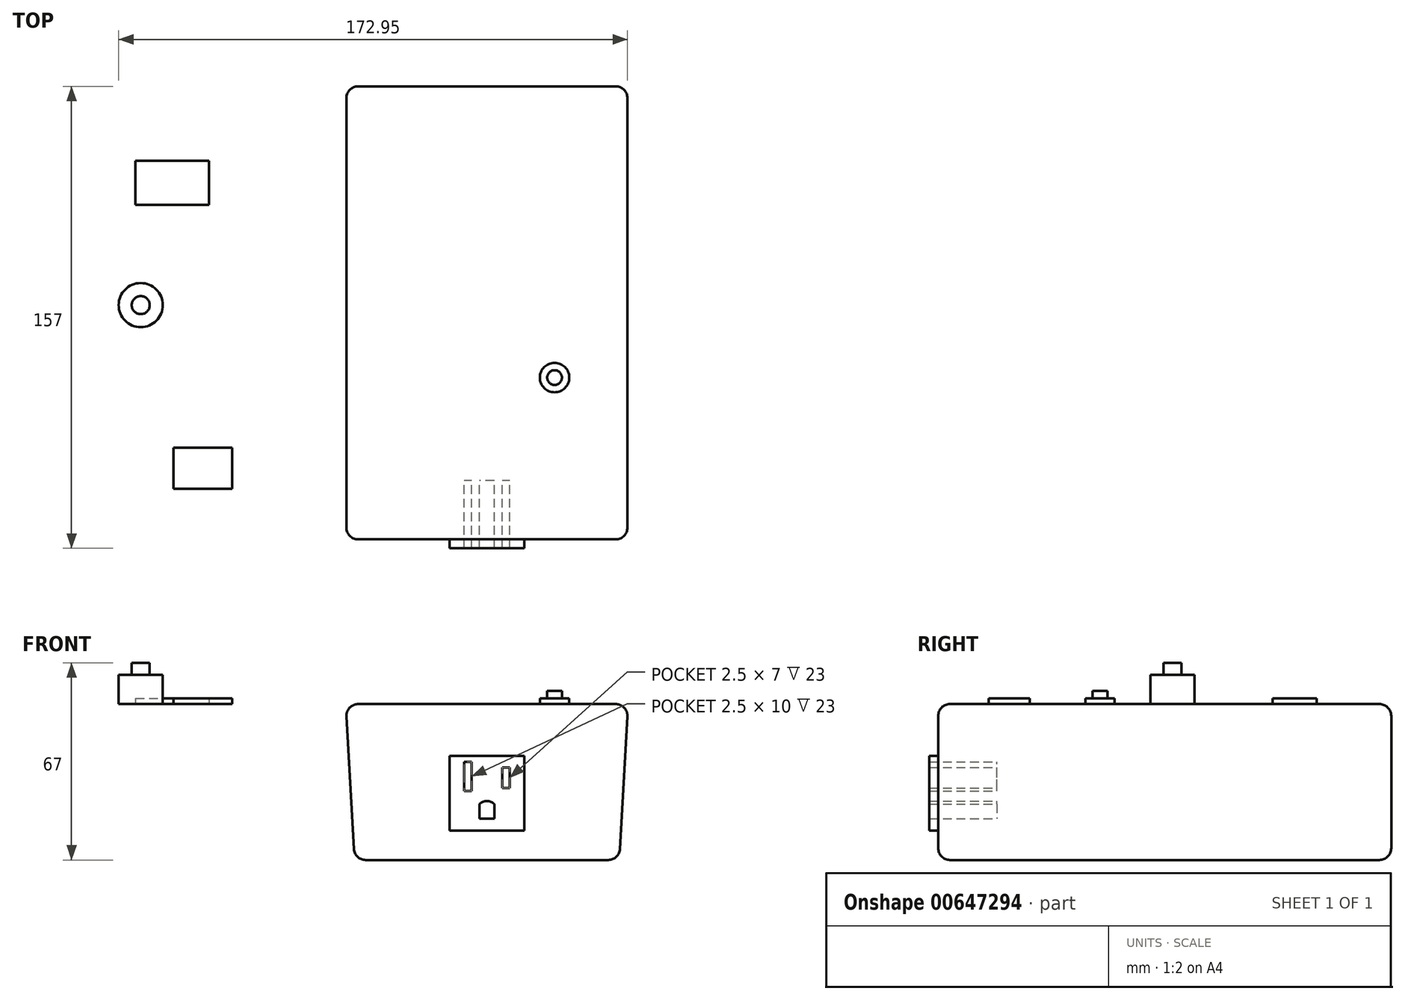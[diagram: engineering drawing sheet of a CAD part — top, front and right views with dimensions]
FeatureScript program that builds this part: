
annotation { "Feature Type Name" : "Feature", "Feature Type Description" : "" }
export const myFeature = defineFeature(function(context is Context, id is Id, definition is map)
    precondition{}
    {
        {
            var Q0;
            Q0=qCreatedBy(makeId("Front.planeOp"),FACE);
            var sketch = newSketch(context, id + "F0", { "sketchPlane" : qUnion([Q0])});
            skLineSegment(sketch, "E0", {"start": v(-48, 0) * mm, "end": v(48, 0) * mm});
            skLineSegment(sketch, "E1", {"start": v(-45, -53) * mm, "end": v(45, -53) * mm});
            skLineSegment(sketch, "E2", {"start": v(-48, 0) * mm, "end": v(-45, -53) * mm});
            skLineSegment(sketch, "E3", {"start": v(48, 0) * mm, "end": v(45, -53) * mm});
            skPoint(sketch, "E4", {"position": v(0, 0) * mm});
            skPoint(sketch, "E5", {"position": v(46.5, -26.5) * mm});
            skPoint(sketch, "E6", {"position": v(-46.5, -26.5) * mm});
            skPoint(sketch, "E7", {"position": v(0, -53) * mm});
            skLineSegment(sketch, "E8", {"start": v(0, 0) * mm, "end": v(0, -53) * mm, "construction": true});
            skLineSegment(sketch, "E9", {"start": v(46.5, -26.5) * mm, "end": v(-46.5, -26.5) * mm, "construction": true});
            skSolve(sketch);
        }
        {
            var Q0;
            Q0 = qSketchRegion(id + "F0", true);
            extrude(context, id + "F1", {"entities" : qUnion([Q0]), "depth" : 154 * mm, "offsetDistance" : 25 * mm});
        }
        {
            var Q0;
            Q0=makeQuery(id+"F1.opExtrude","SWEPT_FACE",FACE,{"disambiguationData":[OSD([sQuery(id+"F0.wireOp",EDGE,"E0")])]});
            var sketch = newSketch(context, id + "F2", { "sketchPlane" : qUnion([Q0])});
            skCircle(sketch, "E10", {"center": v(-23, -99) * mm, "radius": 7.5 * mm});
            skCircle(sketch, "E11", {"center": v(-23, -99) * mm, "radius": 3.06 * mm});
            skCircle(sketch, "E12", {"center": v(23, -99) * mm, "radius": 5 * mm});
            skCircle(sketch, "E13", {"center": v(23, -99) * mm, "radius": 2.5 * mm});
            skLineSegment(sketch, "E14.bottom", {"start": v(-10, -120) * mm, "end": v(10, -120) * mm});
            skLineSegment(sketch, "E14.top", {"start": v(-10, -134) * mm, "end": v(10, -134) * mm});
            skLineSegment(sketch, "E14.left", {"start": v(-10, -120) * mm, "end": v(-10, -134) * mm});
            skLineSegment(sketch, "E14.right", {"start": v(10, -120) * mm, "end": v(10, -134) * mm});
            skLineSegment(sketch, "E15", {"start": v(10, -127) * mm, "end": v(48, -127) * mm, "construction": true});
            skLineSegment(sketch, "E16", {"start": v(-10, -127) * mm, "end": v(-48, -127) * mm, "construction": true});
            skLineSegment(sketch, "E17.bottom", {"start": v(-12.5, -35) * mm, "end": v(12.5, -35) * mm});
            skLineSegment(sketch, "E17.top", {"start": v(-12.5, -50) * mm, "end": v(12.5, -50) * mm});
            skLineSegment(sketch, "E17.left", {"start": v(-12.5, -35) * mm, "end": v(-12.5, -50) * mm});
            skLineSegment(sketch, "E17.right", {"start": v(12.5, -35) * mm, "end": v(12.5, -50) * mm});
            skLineSegment(sketch, "E18", {"start": v(12.5, -42.5) * mm, "end": v(48, -42.5) * mm, "construction": true});
            skLineSegment(sketch, "E19", {"start": v(-12.5, -42.5) * mm, "end": v(-48, -42.5) * mm, "construction": true});
            skSolve(sketch);
        }
        {
            var Q0;
            Q0=makeQuery(id+"F2.imprint","IMPRINT",FACE,{"disambiguationData":[TD([[makeQuery(id+"F2.imprint","IMPRINT",EDGE,{"derivedFrom":sQuery(id+"F2.wireOp",EDGE,"E13")}),1.0]])]});
            extrude(context, id + "F3", {"entities" : qUnion([Q0]), "operationType" : NewBodyOperationType.ADD, "depth" : 4.5 * mm, "offsetDistance" : 25 * mm});
        }
        {
            var Q0;
            Q0=makeQuery(id+"F2.imprint","IMPRINT",FACE,{"disambiguationData":[TD([[makeQuery(id+"F2.imprint","IMPRINT",EDGE,{"derivedFrom":sQuery(id+"F2.wireOp",EDGE,"E12")}),1.0]])]});
            extrude(context, id + "F4", {"entities" : qUnion([Q0]), "operationType" : NewBodyOperationType.ADD, "depth" : 2 * mm, "offsetDistance" : 25 * mm});
        }
        {
            var Q0;
            Q0=makeQuery(id+"F2.imprint","IMPRINT",FACE,{"disambiguationData":[TD([[makeQuery(id+"F2.imprint","IMPRINT",EDGE,{"derivedFrom":sQuery(id+"F2.wireOp",EDGE,"E10")}),1.0]])]});
            extrude(context, id + "F5", {"entities" : qUnion([Q0]), "operationType" : NewBodyOperationType.REMOVE, "depth" : 2 * mm, "offsetDistance" : 25 * mm});
        }
        {
            var Q0;
            Q0=makeQuery(id+"F1.opExtrude","SWEPT_EDGE",EDGE,{"disambiguationData":[OSD([sQuery(id+"F0.wireOp",EDGE,"E1"),sQuery(id+"F0.wireOp",EDGE,"E2")])]});
            var Q1;
            Q1=makeQuery(id+"F1.opExtrude","CAP_EDGE",EDGE,{"disambiguationData":[OSD([sQuery(id+"F0.wireOp",EDGE,"E1")])],"isStart":false});
            var Q2;
            Q2=makeQuery(id+"F1.opExtrude","SWEPT_EDGE",EDGE,{"disambiguationData":[OSD([sQuery(id+"F0.wireOp",EDGE,"E1"),sQuery(id+"F0.wireOp",EDGE,"E3")])]});
            var Q3;
            Q3=makeQuery(id+"F1.opExtrude","CAP_EDGE",EDGE,{"disambiguationData":[OSD([sQuery(id+"F0.wireOp",EDGE,"E1")])],"isStart":true});
            fillet(context, id + "F6", {"entities" : qUnion([Q0, Q1, Q2, Q3]), "radius" : 4 * mm, "tangentPropagation" : true, "allowEdgeOverflow" : false});
        }
        {
            var Q0;
            Q0=makeQuery(id+"F1.opExtrude","CAP_EDGE",EDGE,{"disambiguationData":[OSD([sQuery(id+"F0.wireOp",EDGE,"E0")])],"isStart":false});
            var Q1;
            Q1=makeQuery(id+"F1.opExtrude","CAP_EDGE",EDGE,{"disambiguationData":[OSD([sQuery(id+"F0.wireOp",EDGE,"E3")])],"isStart":false});
            var Q2;
            Q2=makeQuery(id+"F1.opExtrude","CAP_EDGE",EDGE,{"disambiguationData":[OSD([sQuery(id+"F0.wireOp",EDGE,"E2")])],"isStart":false});
            var Q3;
            Q3=makeQuery(id+"F1.opExtrude","CAP_EDGE",EDGE,{"disambiguationData":[OSD([sQuery(id+"F0.wireOp",EDGE,"E2")])],"isStart":true});
            var Q4;
            Q4=makeQuery(id+"F1.opExtrude","SWEPT_EDGE",EDGE,{"disambiguationData":[OSD([sQuery(id+"F0.wireOp",EDGE,"E0"),sQuery(id+"F0.wireOp",EDGE,"E2")])]});
            var Q5;
            Q5=makeQuery(id+"F1.opExtrude","CAP_EDGE",EDGE,{"disambiguationData":[OSD([sQuery(id+"F0.wireOp",EDGE,"E0")])],"isStart":true});
            var Q6;
            Q6=makeQuery(id+"F1.opExtrude","CAP_EDGE",EDGE,{"disambiguationData":[OSD([sQuery(id+"F0.wireOp",EDGE,"E3")])],"isStart":true});
            var Q7;
            Q7=makeQuery(id+"F1.opExtrude","SWEPT_EDGE",EDGE,{"disambiguationData":[OSD([sQuery(id+"F0.wireOp",EDGE,"E0"),sQuery(id+"F0.wireOp",EDGE,"E3")])]});
            fillet(context, id + "F7", {"entities" : qUnion([Q0, Q1, Q2, Q3, Q4, Q5, Q6, Q7]), "radius" : 4 * mm, "tangentPropagation" : true, "allowEdgeOverflow" : false});
        }
        {
            var Q0;
            Q0=makeQuery(id+"F1.opExtrude","CAP_FACE",FACE,{"disambiguationData":[OSD([sQuery(id+"F0.wireOp",EDGE,"E0"),sQuery(id+"F0.wireOp",EDGE,"E1"),sQuery(id+"F0.wireOp",EDGE,"E2"),sQuery(id+"F0.wireOp",EDGE,"E3")])],"isStart":false});
            var sketch = newSketch(context, id + "F8", { "sketchPlane" : qUnion([Q0])});
            skLineSegment(sketch, "E20.bottom", {"start": v(12.7, -17.6) * mm, "end": v(-12.7, -17.6) * mm});
            skLineSegment(sketch, "E20.top", {"start": v(12.7, -43) * mm, "end": v(-12.7, -43) * mm});
            skLineSegment(sketch, "E20.left", {"start": v(12.7, -17.6) * mm, "end": v(12.7, -43) * mm});
            skLineSegment(sketch, "E20.right", {"start": v(-12.7, -17.6) * mm, "end": v(-12.7, -43) * mm});
            skPoint(sketch, "E20.middle", {"position": v(0, -30.3) * mm});
            skLineSegment(sketch, "E21.bottom", {"start": v(-5.2, -29.6) * mm, "end": v(-7.7, -29.6) * mm});
            skLineSegment(sketch, "E21.top", {"start": v(-5.2, -19.6) * mm, "end": v(-7.7, -19.6) * mm});
            skLineSegment(sketch, "E21.left", {"start": v(-5.2, -29.6) * mm, "end": v(-5.2, -19.6) * mm});
            skLineSegment(sketch, "E21.right", {"start": v(-7.7, -29.6) * mm, "end": v(-7.7, -19.6) * mm});
            skPoint(sketch, "E21.middle", {"position": v(-6.45, -24.6) * mm});
            skLineSegment(sketch, "E22.bottom", {"start": v(7.7, -28.6) * mm, "end": v(5.2, -28.6) * mm});
            skLineSegment(sketch, "E22.top", {"start": v(7.7, -21.6) * mm, "end": v(5.2, -21.6) * mm});
            skLineSegment(sketch, "E22.left", {"start": v(7.7, -28.6) * mm, "end": v(7.7, -21.6) * mm});
            skLineSegment(sketch, "E22.right", {"start": v(5.2, -28.6) * mm, "end": v(5.2, -21.6) * mm});
            skLineSegment(sketch, "E23.top", {"start": v(2.5, -39) * mm, "end": v(-2.5, -39) * mm});
            skLineSegment(sketch, "E23.left", {"start": v(2.5, -34) * mm, "end": v(2.5, -39) * mm});
            skLineSegment(sketch, "E23.right", {"start": v(-2.5, -34) * mm, "end": v(-2.5, -39) * mm});
            skPoint(sketch, "E23.middle", {"position": v(0, -36.5) * mm});
            skArc(sketch, "E24", {"start": v(2.5, -34) * mm, "mid": v(0, -32.96) * mm, "end": v(-2.5, -34) * mm});
            skSolve(sketch);
        }
        {
            var Q0;
            Q0=makeQuery(id+"F8.imprint","IMPRINT",FACE,{"disambiguationData":[TD([[makeQuery(id+"F8.imprint","IMPRINT",EDGE,{"derivedFrom":sQuery(id+"F8.wireOp",EDGE,"E20.bottom")}),1.0]])]});
            extrude(context, id + "F9", {"entities" : qUnion([Q0]), "operationType" : NewBodyOperationType.ADD, "depth" : 3 * mm, "offsetDistance" : 25 * mm});
        }
        {
            var Q0;
            Q0=makeQuery(id+"F9.boolean.opBoolean","SPLIT",FACE,{"disambiguationData":[TD([makeQuery(id+"F9.opExtrude","SWEPT_FACE",FACE,{"disambiguationData":[OSD([sQuery(id+"F8.wireOp",EDGE,"E21.bottom")])]})])],"derivedFrom":makeQuery(id+"F1.opExtrude","CAP_FACE",FACE,{"disambiguationData":[OSD([sQuery(id+"F0.wireOp",EDGE,"E0"),sQuery(id+"F0.wireOp",EDGE,"E1"),sQuery(id+"F0.wireOp",EDGE,"E2"),sQuery(id+"F0.wireOp",EDGE,"E3")])],"isStart":false})});
            var Q1;
            Q1=makeQuery(id+"F9.boolean.opBoolean","SPLIT",FACE,{"disambiguationData":[TD([makeQuery(id+"F9.opExtrude","SWEPT_FACE",FACE,{"disambiguationData":[OSD([sQuery(id+"F8.wireOp",EDGE,"E22.bottom")])]})])],"derivedFrom":makeQuery(id+"F1.opExtrude","CAP_FACE",FACE,{"disambiguationData":[OSD([sQuery(id+"F0.wireOp",EDGE,"E0"),sQuery(id+"F0.wireOp",EDGE,"E1"),sQuery(id+"F0.wireOp",EDGE,"E2"),sQuery(id+"F0.wireOp",EDGE,"E3")])],"isStart":false})});
            var Q2;
            Q2=makeQuery(id+"F9.boolean.opBoolean","SPLIT",FACE,{"disambiguationData":[TD([makeQuery(id+"F9.opExtrude","SWEPT_FACE",FACE,{"disambiguationData":[OSD([sQuery(id+"F8.wireOp",EDGE,"E23.top")])]})])],"derivedFrom":makeQuery(id+"F1.opExtrude","CAP_FACE",FACE,{"disambiguationData":[OSD([sQuery(id+"F0.wireOp",EDGE,"E0"),sQuery(id+"F0.wireOp",EDGE,"E1"),sQuery(id+"F0.wireOp",EDGE,"E2"),sQuery(id+"F0.wireOp",EDGE,"E3")])],"isStart":false})});
            extrude(context, id + "F10", {"entities" : qUnion([Q0, Q1, Q2]), "operationType" : NewBodyOperationType.REMOVE, "oppositeDirection" : true, "depth" : 20 * mm, "offsetDistance" : 25 * mm});
        }
        {
            var Q0;
            Q0=qCreatedBy(makeId("Top.planeOp"),FACE);
            var sketch = newSketch(context, id + "F11", { "sketchPlane" : qUnion([Q0])});
            skLineSegment(sketch, "E25.bottom", {"start": v(-119.45, -25.34) * mm, "end": v(-94.45, -25.34) * mm});
            skLineSegment(sketch, "E25.top", {"start": v(-119.45, -40.34) * mm, "end": v(-94.45, -40.34) * mm});
            skLineSegment(sketch, "E25.left", {"start": v(-119.45, -25.34) * mm, "end": v(-119.45, -40.34) * mm});
            skLineSegment(sketch, "E25.right", {"start": v(-94.45, -25.34) * mm, "end": v(-94.45, -40.34) * mm});
            skSolve(sketch);
        }
        {
            var Q0;
            Q0=makeQuery(id+"F11.imprint","IMPRINT",FACE,{"disambiguationData":[TD([[makeQuery(id+"F11.imprint","IMPRINT",EDGE,{"derivedFrom":sQuery(id+"F11.wireOp",EDGE,"E25.bottom")}),-1.0]])]});
            extrude(context, id + "F12", {"entities" : qUnion([Q0]), "depth" : 2 * mm, "offsetDistance" : 25 * mm});
        }
        {
            var Q0;
            Q0=makeQuery(id+"F12.opExtrude","SWEPT_BODY",BODY,{"disambiguationData":[OSD([sQuery(id+"F11.wireOp",EDGE,"E25.bottom"),sQuery(id+"F11.wireOp",EDGE,"E25.top"),sQuery(id+"F11.wireOp",EDGE,"E25.left"),sQuery(id+"F11.wireOp",EDGE,"E25.right")])]});
            transform(context, id + "F13", {"entities" : qUnion([Q0]), "transformType" : TransformType.TRANSLATION_3D, "dx" : 0 * mm, "dy" : -106 * mm, "dz" : 0 * mm, "makeCopy" : true});
        }
        {
            var Q0;
            Q0=makeQuery(id+"F13.opPattern","COPY",BODY,{"derivedFrom":makeQuery(id+"F12.opExtrude","SWEPT_BODY",BODY,{"disambiguationData":[OSD([sQuery(id+"F11.wireOp",EDGE,"E25.bottom"),sQuery(id+"F11.wireOp",EDGE,"E25.top"),sQuery(id+"F11.wireOp",EDGE,"E25.left"),sQuery(id+"F11.wireOp",EDGE,"E25.right")])]}),"instanceName":"1"});
            deleteBodies(context, id + "F14", {"entities" : qUnion([Q0])});
        }
        {
            var Q0;
            Q0=qCreatedBy(makeId("Top.planeOp"),FACE);
            var sketch = newSketch(context, id + "F15", { "sketchPlane" : qUnion([Q0])});
            skLineSegment(sketch, "E26.bottom", {"start": v(-106.58, -122.86) * mm, "end": v(-86.58, -122.86) * mm});
            skLineSegment(sketch, "E26.top", {"start": v(-106.58, -136.86) * mm, "end": v(-86.58, -136.86) * mm});
            skLineSegment(sketch, "E26.left", {"start": v(-106.58, -122.86) * mm, "end": v(-106.58, -136.86) * mm});
            skLineSegment(sketch, "E26.right", {"start": v(-86.58, -122.86) * mm, "end": v(-86.58, -136.86) * mm});
            skSolve(sketch);
        }
        {
            var Q0;
            Q0 = qSketchRegion(id + "F15", true);
            extrude(context, id + "F16", {"entities" : qUnion([Q0]), "depth" : 2 * mm, "offsetDistance" : 25 * mm});
        }
        {
            var Q0;
            Q0=qCreatedBy(makeId("Top.planeOp"),FACE);
            var sketch = newSketch(context, id + "F17", { "sketchPlane" : qUnion([Q0])});
            skCircle(sketch, "E27", {"center": v(-117.68, -74.37) * mm, "radius": 7.5 * mm});
            skCircle(sketch, "E28", {"center": v(-117.68, -74.37) * mm, "radius": 3.06 * mm});
            skSolve(sketch);
        }
        {
            var Q0;
            Q0 = qSketchRegion(id + "F17", true);
            extrude(context, id + "F18", {"entities" : qUnion([Q0]), "depth" : 10 * mm, "offsetDistance" : 25 * mm});
        }
        {
            var Q0;
            Q0=makeQuery(id+"F17.imprint","IMPRINT",FACE,{"disambiguationData":[TD([[makeQuery(id+"F17.imprint","IMPRINT",EDGE,{"derivedFrom":sQuery(id+"F17.wireOp",EDGE,"E28")}),1.0]])]});
            extrude(context, id + "F19", {"entities" : qUnion([Q0]), "operationType" : NewBodyOperationType.ADD, "depth" : 14 * mm, "offsetDistance" : 25 * mm});
        }
    });
